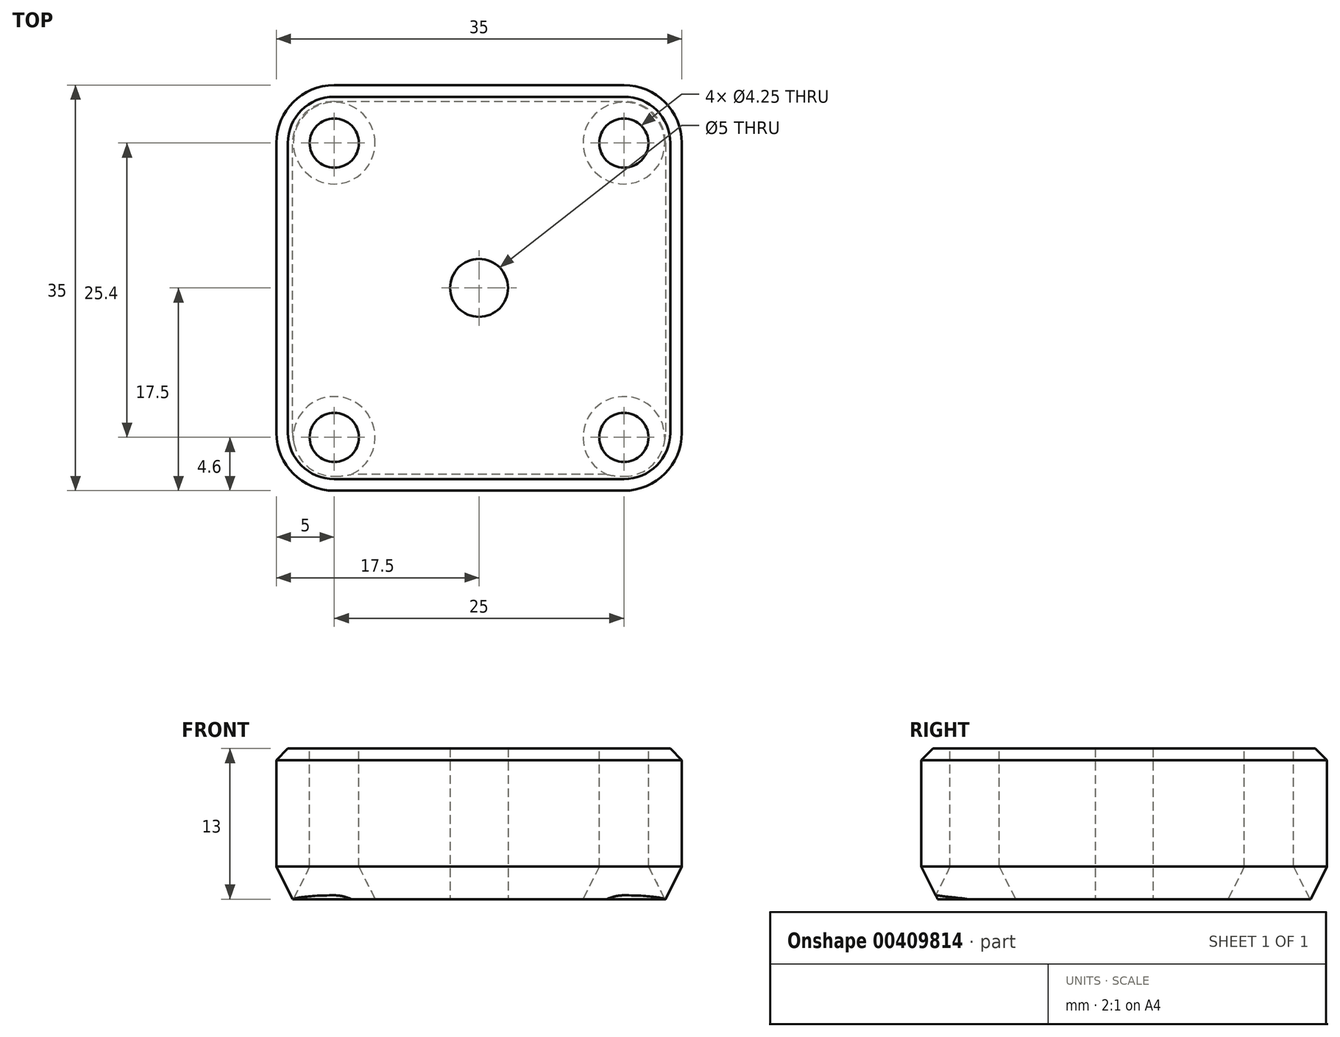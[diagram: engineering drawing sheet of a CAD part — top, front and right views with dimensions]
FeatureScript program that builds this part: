
annotation { "Feature Type Name" : "Feature", "Feature Type Description" : "" }
export const myFeature = defineFeature(function(context is Context, id is Id, definition is map)
    precondition{}
    {
        {
            var Q0;
            Q0=qCreatedBy(makeId("Top.planeOp"),FACE);
            var sketch = newSketch(context, id + "F0", { "sketchPlane" : qUnion([Q0])});
            skLineSegment(sketch, "E0.bottom", {"start": v(17.5, 17.5) * mm, "end": v(-17.5, 17.5) * mm});
            skLineSegment(sketch, "E0.top", {"start": v(17.5, -17.5) * mm, "end": v(-17.5, -17.5) * mm});
            skLineSegment(sketch, "E0.left", {"start": v(17.5, 17.5) * mm, "end": v(17.5, -17.5) * mm});
            skLineSegment(sketch, "E0.right", {"start": v(-17.5, 17.5) * mm, "end": v(-17.5, -17.5) * mm});
            skPoint(sketch, "E0.middle", {"position": v(0, 0) * mm});
            skSolve(sketch);
        }
        {
            var Q0;
            Q0=makeQuery(id+"F0.imprint","IMPRINT",FACE,{"disambiguationData":[TD([[makeQuery(id+"F0.imprint","IMPRINT",EDGE,{"derivedFrom":sQuery(id+"F0.wireOp",EDGE,"E0.bottom")}),1.0]])]});
            extrude(context, id + "F1", {"entities" : qUnion([Q0]), "endBound" : BoundingType.SYMMETRIC, "depth" : 13 * mm});
        }
        {
            var Q0;
            Q0=makeQuery(id+"F1.opExtrude","CAP_FACE",FACE,{"disambiguationData":[OSD([sQuery(id+"F0.wireOp",EDGE,"E0.bottom"),sQuery(id+"F0.wireOp",EDGE,"E0.top"),sQuery(id+"F0.wireOp",EDGE,"E0.left"),sQuery(id+"F0.wireOp",EDGE,"E0.right")])],"isStart":false});
            var sketch = newSketch(context, id + "F2", { "sketchPlane" : qUnion([Q0])});
            skCircle(sketch, "E1", {"center": v(-12.5, -12.9) * mm, "radius": 2.12 * mm});
            skCircle(sketch, "E2", {"center": v(-12.5, 12.5) * mm, "radius": 2.12 * mm});
            skCircle(sketch, "E3", {"center": v(12.5, 12.5) * mm, "radius": 2.12 * mm});
            skCircle(sketch, "E4", {"center": v(12.5, -12.9) * mm, "radius": 2.12 * mm});
            skSolve(sketch);
        }
        {
            var Q0;
            Q0=qSketchRegion(id+"F2",true);
            extrude(context, id + "F3", {"entities" : qUnion([Q0]), "operationType" : NewBodyOperationType.REMOVE, "endBound" : BoundingType.THROUGH_ALL, "oppositeDirection" : true, "depth" : 25 * mm});
        }
        {
            var Q0;
            Q0=makeQuery(id+"F1.opExtrude","SWEPT_EDGE",EDGE,{"disambiguationData":[OSD([sQuery(id+"F0.wireOp",EDGE,"E0.bottom"),sQuery(id+"F0.wireOp",EDGE,"E0.right")])]});
            var Q1;
            Q1=makeQuery(id+"F1.opExtrude","SWEPT_EDGE",EDGE,{"disambiguationData":[OSD([sQuery(id+"F0.wireOp",EDGE,"E0.bottom"),sQuery(id+"F0.wireOp",EDGE,"E0.left")])]});
            var Q2;
            Q2=makeQuery(id+"F1.opExtrude","SWEPT_EDGE",EDGE,{"disambiguationData":[OSD([sQuery(id+"F0.wireOp",EDGE,"E0.top"),sQuery(id+"F0.wireOp",EDGE,"E0.left")])]});
            var Q3;
            Q3=makeQuery(id+"F1.opExtrude","SWEPT_EDGE",EDGE,{"disambiguationData":[OSD([sQuery(id+"F0.wireOp",EDGE,"E0.top"),sQuery(id+"F0.wireOp",EDGE,"E0.right")])]});
            fillet(context, id + "F4", {"entities" : qUnion([Q0, Q1, Q2, Q3]), "radius" : 5 * mm, "tangentPropagation" : true, "allowEdgeOverflow" : false});
        }
        {
            var Q0;
            Q0=makeQuery(id+"F3.boolean.opBoolean","INTERSECT",EDGE,{"derivedFrom":[makeQuery(id+"F1.opExtrude","CAP_FACE",FACE,{"disambiguationData":[OSD([sQuery(id+"F0.wireOp",EDGE,"E0.bottom"),sQuery(id+"F0.wireOp",EDGE,"E0.top"),sQuery(id+"F0.wireOp",EDGE,"E0.left"),sQuery(id+"F0.wireOp",EDGE,"E0.right")])],"isStart":true}),makeQuery(id+"F3.opExtrude","SWEPT_FACE",FACE,{"disambiguationData":[OSD([sQuery(id+"F2.wireOp",EDGE,"E1")])]})]});
            var Q1;
            Q1=makeQuery(id+"F3.boolean.opBoolean","INTERSECT",EDGE,{"derivedFrom":[makeQuery(id+"F1.opExtrude","CAP_FACE",FACE,{"disambiguationData":[OSD([sQuery(id+"F0.wireOp",EDGE,"E0.bottom"),sQuery(id+"F0.wireOp",EDGE,"E0.top"),sQuery(id+"F0.wireOp",EDGE,"E0.left"),sQuery(id+"F0.wireOp",EDGE,"E0.right")])],"isStart":true}),makeQuery(id+"F3.opExtrude","SWEPT_FACE",FACE,{"disambiguationData":[OSD([sQuery(id+"F2.wireOp",EDGE,"E4")])]})]});
            var Q2;
            Q2=makeQuery(id+"F3.boolean.opBoolean","INTERSECT",EDGE,{"derivedFrom":[makeQuery(id+"F1.opExtrude","CAP_FACE",FACE,{"disambiguationData":[OSD([sQuery(id+"F0.wireOp",EDGE,"E0.bottom"),sQuery(id+"F0.wireOp",EDGE,"E0.top"),sQuery(id+"F0.wireOp",EDGE,"E0.left"),sQuery(id+"F0.wireOp",EDGE,"E0.right")])],"isStart":true}),makeQuery(id+"F3.opExtrude","SWEPT_FACE",FACE,{"disambiguationData":[OSD([sQuery(id+"F2.wireOp",EDGE,"E3")])]})]});
            var Q3;
            Q3=makeQuery(id+"F1.opExtrude","CAP_FACE",FACE,{"disambiguationData":[OSD([sQuery(id+"F0.wireOp",EDGE,"E0.bottom"),sQuery(id+"F0.wireOp",EDGE,"E0.top"),sQuery(id+"F0.wireOp",EDGE,"E0.left"),sQuery(id+"F0.wireOp",EDGE,"E0.right")])],"isStart":true});
            chamfer(context, id + "F5", {"entities" : qUnion([Q0, Q1, Q2, Q3]), "chamferType" : ChamferType.TWO_OFFSETS, "width1" : 1.4 * mm, "oppositeDirection" : false, "width2" : 2.8 * mm, "tangentPropagation" : true});
        }
        {
            var Q0;
            Q0=makeQuery(id+"F1.opExtrude","CAP_FACE",FACE,{"disambiguationData":[OSD([sQuery(id+"F0.wireOp",EDGE,"E0.bottom"),sQuery(id+"F0.wireOp",EDGE,"E0.top"),sQuery(id+"F0.wireOp",EDGE,"E0.left"),sQuery(id+"F0.wireOp",EDGE,"E0.right")])],"isStart":true});
            var sketch = newSketch(context, id + "F6", { "sketchPlane" : qUnion([Q0])});
            skCircle(sketch, "E5", {"center": v(0, 0) * mm, "radius": 2.5 * mm});
            skSolve(sketch);
        }
        {
            var Q0;
            Q0=qSketchRegion(id+"F6",true);
            extrude(context, id + "F7", {"entities" : qUnion([Q0]), "operationType" : NewBodyOperationType.REMOVE, "endBound" : BoundingType.THROUGH_ALL, "oppositeDirection" : true, "depth" : 25 * mm});
        }
        {
            var Q0;
            Q0=makeQuery(id+"F1.opExtrude","CAP_EDGE",EDGE,{"disambiguationData":[OSD([sQuery(id+"F0.wireOp",EDGE,"E0.right")])],"isStart":false});
            chamfer(context, id + "F8", {"entities" : qUnion([Q0]), "width" : 1 * mm, "tangentPropagation" : true});
        }
    });
